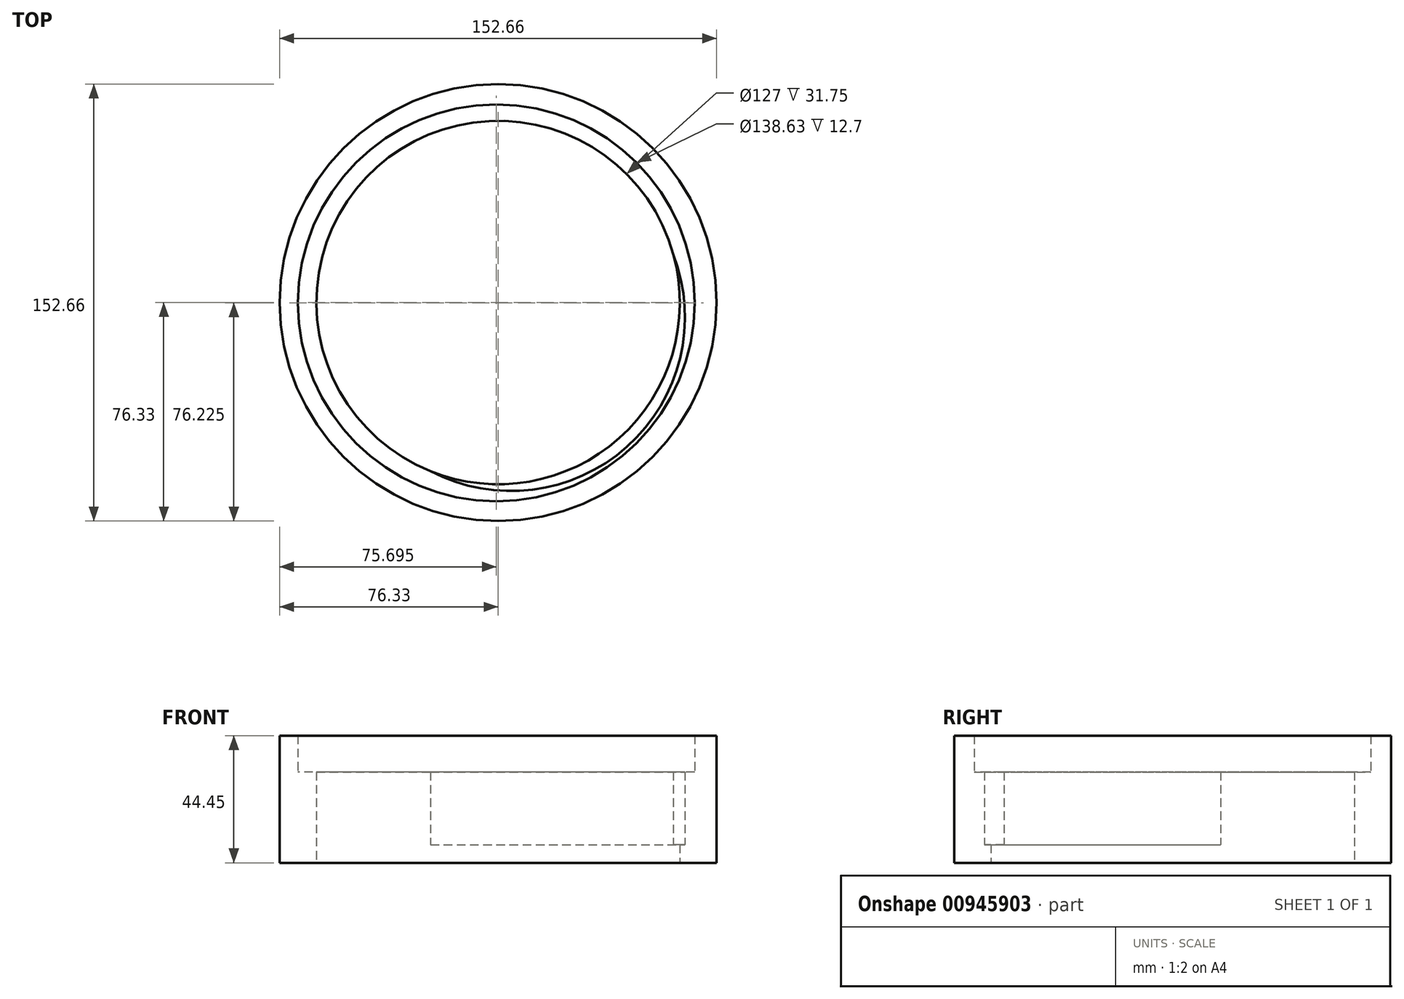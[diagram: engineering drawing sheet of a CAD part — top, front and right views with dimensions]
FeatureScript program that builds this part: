
annotation { "Feature Type Name" : "Feature", "Feature Type Description" : "" }
export const myFeature = defineFeature(function(context is Context, id is Id, definition is map)
    precondition{}
    {
        {
            var Q0;
            Q0=qCreatedBy(makeId("Top.planeOp"),FACE);
            var sketch = newSketch(context, id + "F0", { "sketchPlane" : qUnion([Q0])});
            skCircle(sketch, "E0", {"center": v(0, 0) * mm, "radius": 76.33 * mm});
            skCircle(sketch, "E1", {"center": v(0, 0) * mm, "radius": 63.5 * mm});
            skCircle(sketch, "E2", {"center": v(0, 0) * mm, "radius": 48.8 * mm});
            skSolve(sketch);
        }
        {
            var Q0;
            Q0=makeQuery(id+"F0.imprint","IMPRINT",FACE,{"disambiguationData":[TD([[makeQuery(id+"F0.imprint","IMPRINT",EDGE,{"derivedFrom":sQuery(id+"F0.wireOp",EDGE,"E0")}),1.0]])]});
            extrude(context, id + "F1", {"entities" : qUnion([Q0]), "depth" : 6.35 * mm, "offsetDistance" : 25.4 * mm});
        }
        {
            var Q0;
            Q0=makeQuery(id+"F1.opExtrude","CAP_FACE",FACE,{"disambiguationData":[OSD([sQuery(id+"F0.wireOp",EDGE,"E0"),sQuery(id+"F0.wireOp",EDGE,"E1")])],"isStart":false});
            var sketch = newSketch(context, id + "F2", { "sketchPlane" : qUnion([Q0])});
            skCircle(sketch, "E3", {"center": v(4.5, -5.05) * mm, "radius": 60.8 * mm});
            skSolve(sketch);
        }
        {
            var Q0;
            Q0=makeQuery(id+"F2.imprint","IMPRINT",FACE,{"disambiguationData":[TD([[makeQuery(id+"F2.imprint","IMPRINT",EDGE,{"derivedFrom":makeQuery(id+"F1.opExtrude","CAP_EDGE",EDGE,{"disambiguationData":[OSD([sQuery(id+"F0.wireOp",EDGE,"E0")])],"isStart":false})}),1.0]])]});
            extrude(context, id + "F3", {"entities" : qUnion([Q0]), "operationType" : NewBodyOperationType.ADD, "depth" : 25.4 * mm, "offsetDistance" : 25.4 * mm});
        }
        {
            var Q0;
            Q0=makeQuery(id+"F3.opExtrude","CAP_FACE",FACE,{"disambiguationData":[OSD([sQuery(id+"F0.wireOp",EDGE,"E0"),sQuery(id+"F0.wireOp",EDGE,"E1"),sQuery(id+"F2.wireOp",EDGE,"E3")])],"isStart":false});
            var sketch = newSketch(context, id + "F4", { "sketchPlane" : qUnion([Q0])});
            skCircle(sketch, "E4", {"center": v(-0.64, -0.1) * mm, "radius": 69.32 * mm});
            skPoint(sketch, "E4.first.point", {"position": v(68.68, 0) * mm});
            skPoint(sketch, "E4.second.point", {"position": v(-69.95, 0) * mm});
            skPoint(sketch, "E4.third.point", {"position": v(-15.54, 67.6) * mm});
            skSolve(sketch);
        }
        {
            var Q0;
            Q0=makeQuery(id+"F4.imprint","IMPRINT",FACE,{"disambiguationData":[TD([[makeQuery(id+"F4.imprint","IMPRINT",EDGE,{"derivedFrom":sQuery(id+"F4.wireOp",EDGE,"E4")}),-1.0]])]});
            extrude(context, id + "F5", {"entities" : qUnion([Q0]), "operationType" : NewBodyOperationType.ADD, "depth" : 12.7 * mm, "offsetDistance" : 25.4 * mm});
        }
    });
